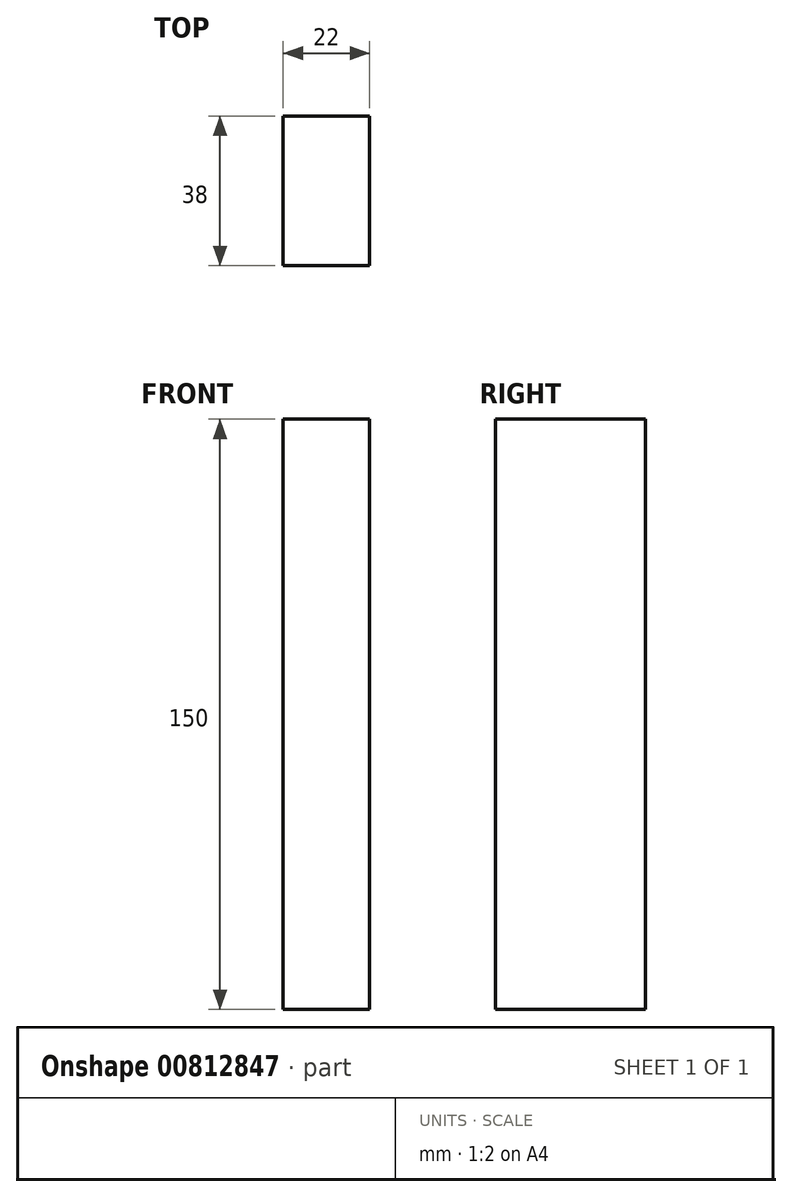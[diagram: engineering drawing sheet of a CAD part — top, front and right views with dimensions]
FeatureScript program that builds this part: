
annotation { "Feature Type Name" : "Feature", "Feature Type Description" : "" }
export const myFeature = defineFeature(function(context is Context, id is Id, definition is map)
    precondition{}
    {
        {
            var Q0;
            Q0=qCreatedBy(makeId("Top.planeOp"),FACE);
            var sketch = newSketch(context, id + "F0", { "sketchPlane" : qUnion([Q0])});
            skLineSegment(sketch, "E0.bottom", {"start": v(-18.88, 28.95) * mm, "end": v(-40.88, 28.95) * mm});
            skLineSegment(sketch, "E0.top", {"start": v(-18.88, 66.95) * mm, "end": v(-40.88, 66.95) * mm});
            skLineSegment(sketch, "E0.left", {"start": v(-18.88, 28.95) * mm, "end": v(-18.88, 66.95) * mm});
            skLineSegment(sketch, "E0.right", {"start": v(-40.88, 28.95) * mm, "end": v(-40.88, 66.95) * mm});
            skPoint(sketch, "E0.middle", {"position": v(-29.88, 47.95) * mm});
            skSolve(sketch);
        }
        {
            var Q0;
            Q0=makeQuery(id+"F0.imprint","IMPRINT",FACE,{"disambiguationData":[TD([[makeQuery(id+"F0.imprint","IMPRINT",EDGE,{"derivedFrom":sQuery(id+"F0.wireOp",EDGE,"E0.bottom")}),-1.0]])]});
            extrude(context, id + "F1", {"entities" : qUnion([Q0]), "depth" : 150 * mm, "offsetDistance" : 25 * mm});
        }
    });
